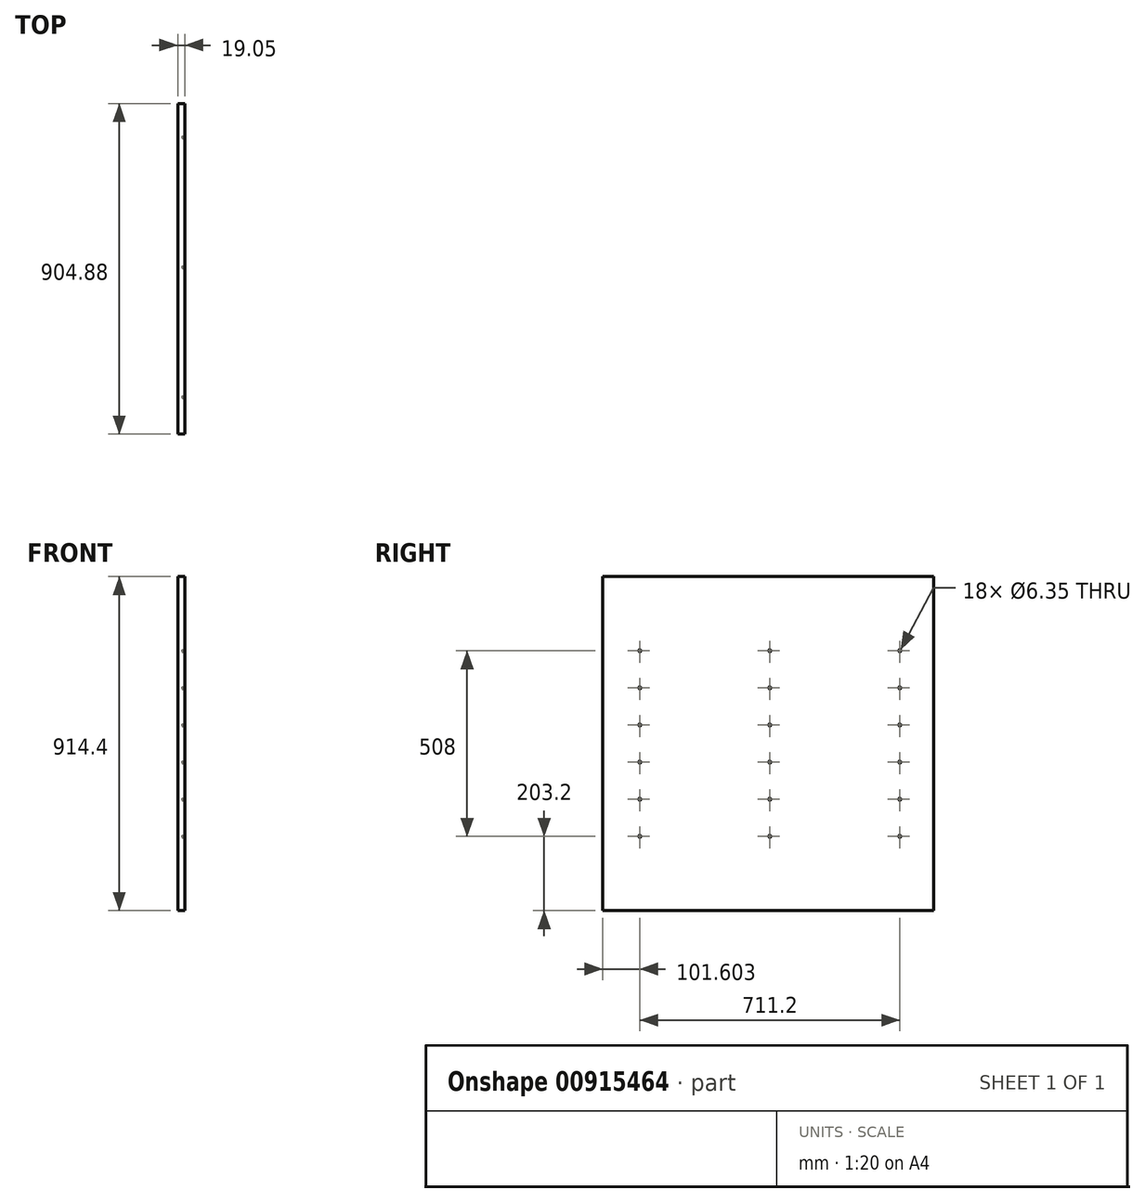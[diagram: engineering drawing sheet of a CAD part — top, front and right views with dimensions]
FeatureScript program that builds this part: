
annotation { "Feature Type Name" : "Feature", "Feature Type Description" : "" }
export const myFeature = defineFeature(function(context is Context, id is Id, definition is map)
    precondition{}
    {
        {
            var Q0;
            Q0=qCreatedBy(makeId("Right.planeOp"),FACE);
            var sketch = newSketch(context, id + "F0", { "sketchPlane" : qUnion([Q0])});
            skLineSegment(sketch, "E0.bottom", {"start": v(452.44, 457.2) * mm, "end": v(-452.44, 457.2) * mm});
            skLineSegment(sketch, "E0.top", {"start": v(452.44, -457.2) * mm, "end": v(-452.44, -457.2) * mm});
            skLineSegment(sketch, "E0.left", {"start": v(452.44, 457.2) * mm, "end": v(452.44, -457.2) * mm});
            skLineSegment(sketch, "E0.right", {"start": v(-452.44, 457.2) * mm, "end": v(-452.44, -457.2) * mm});
            skPoint(sketch, "E0.middle", {"position": v(0, 0) * mm});
            skSolve(sketch);
        }
        {
            var Q0;
            Q0=makeQuery(id+"F0.imprint","IMPRINT",FACE,{"disambiguationData":[TD([[makeQuery(id+"F0.imprint","IMPRINT",EDGE,{"derivedFrom":sQuery(id+"F0.wireOp",EDGE,"E0.bottom")}),1.0]])]});
            extrude(context, id + "F1", {"entities" : qUnion([Q0]), "oppositeDirection" : true, "depth" : 19.05 * mm, "offsetDistance" : 25.4 * mm});
        }
        {
            var Q0;
            Q0=makeQuery(id+"F1.opExtrude","CAP_FACE",FACE,{"disambiguationData":[OSD([sQuery(id+"F0.wireOp",EDGE,"E0.bottom"),sQuery(id+"F0.wireOp",EDGE,"E0.top"),sQuery(id+"F0.wireOp",EDGE,"E0.left"),sQuery(id+"F0.wireOp",EDGE,"E0.right")])],"isStart":true});
            var sketch = newSketch(context, id + "F2", { "sketchPlane" : qUnion([Q0])});
            skPoint(sketch, "E1", {"position": v(-350.84, 254) * mm});
            skPoint(sketch, "E2.0.1.0", {"position": v(-350.84, 152.4) * mm});
            skPoint(sketch, "E2.0.2.0", {"position": v(-350.84, 50.8) * mm});
            skPoint(sketch, "E2.0.3.0", {"position": v(-350.84, -50.8) * mm});
            skPoint(sketch, "E2.0.4.0", {"position": v(-350.84, -152.4) * mm});
            skPoint(sketch, "E2.0.5.0", {"position": v(-350.84, -254) * mm});
            skPoint(sketch, "E2.1.0.0", {"position": v(4.76, 254) * mm});
            skPoint(sketch, "E2.1.1.0", {"position": v(4.76, 152.4) * mm});
            skPoint(sketch, "E2.1.2.0", {"position": v(4.76, 50.8) * mm});
            skPoint(sketch, "E2.1.3.0", {"position": v(4.76, -50.8) * mm});
            skPoint(sketch, "E2.1.4.0", {"position": v(4.76, -152.4) * mm});
            skPoint(sketch, "E2.1.5.0", {"position": v(4.76, -254) * mm});
            skPoint(sketch, "E2.2.0.0", {"position": v(360.36, 254) * mm});
            skPoint(sketch, "E2.2.1.0", {"position": v(360.36, 152.4) * mm});
            skPoint(sketch, "E2.2.2.0", {"position": v(360.36, 50.8) * mm});
            skPoint(sketch, "E2.2.3.0", {"position": v(360.36, -50.8) * mm});
            skPoint(sketch, "E2.2.4.0", {"position": v(360.36, -152.4) * mm});
            skPoint(sketch, "E2.2.5.0", {"position": v(360.36, -254) * mm});
            skLineSegment(sketch, "E2.direction1", {"start": v(-350.84, 254) * mm, "end": v(4.76, 254) * mm, "construction": true});
            skLineSegment(sketch, "E2.direction2", {"start": v(-350.84, 254) * mm, "end": v(-350.84, 152.4) * mm, "construction": true});
            skSolve(sketch);
        }
        {
            var Q0;
            Q0=sQuery(id+"F2.wireOp",VERTEX,"E2.2.5.0");
            var Q1;
            Q1=sQuery(id+"F2.wireOp",VERTEX,"E2.0.4.0");
            var Q2;
            Q2=sQuery(id+"F2.wireOp",VERTEX,"E2.2.0.0");
            var Q3;
            Q3=sQuery(id+"F2.wireOp",VERTEX,"E2.1.0.0");
            var Q4;
            Q4=sQuery(id+"F2.wireOp",VERTEX,"E2.2.4.0");
            var Q5;
            Q5=sQuery(id+"F2.wireOp",VERTEX,"E2.2.1.0");
            var Q6;
            Q6=sQuery(id+"F2.wireOp",VERTEX,"E2.0.5.0");
            var Q7;
            Q7=sQuery(id+"F2.wireOp",VERTEX,"E2.1.1.0");
            var Q8;
            Q8=sQuery(id+"F2.wireOp",VERTEX,"E2.2.3.0");
            var Q9;
            Q9=sQuery(id+"F2.wireOp",VERTEX,"E2.direction2.end");
            var Q10;
            Q10=sQuery(id+"F2.wireOp",VERTEX,"E2.2.2.0");
            var Q11;
            Q11=sQuery(id+"F2.wireOp",VERTEX,"E1");
            var Q12;
            Q12=sQuery(id+"F2.wireOp",VERTEX,"E2.1.4.0");
            var Q13;
            Q13=sQuery(id+"F2.wireOp",VERTEX,"E2.0.3.0");
            var Q14;
            Q14=sQuery(id+"F2.wireOp",VERTEX,"E2.1.3.0");
            var Q15;
            Q15=sQuery(id+"F2.wireOp",VERTEX,"E2.0.2.0");
            var Q16;
            Q16=sQuery(id+"F2.wireOp",VERTEX,"E2.1.2.0");
            var Q17;
            Q17=sQuery(id+"F2.wireOp",VERTEX,"E2.1.5.0");
            var Q18;
            Q18=makeQuery(id+"F1.opExtrude","SWEPT_BODY",BODY,{"disambiguationData":[OSD([sQuery(id+"F0.wireOp",EDGE,"E0.bottom"),sQuery(id+"F0.wireOp",EDGE,"E0.top"),sQuery(id+"F0.wireOp",EDGE,"E0.left"),sQuery(id+"F0.wireOp",EDGE,"E0.right")])]});
            hole(context, id + "F3", {"style" : HoleStyle.SIMPLE, "endStyle" : HoleEndStyle.BLIND, "holeDiameter" : 6.35 * mm, "majorDiameter" : 6.35 * mm, "holeDepth" : 6.35 * mm, "isTappedThrough" : true, "tappedDepth" : 12.7 * mm, "tapClearance" : 3, "startFromSketch" : true, "locations" : qUnion([Q0, Q1, Q2, Q3, Q4, Q5, Q6, Q7, Q8, Q9, Q10, Q11, Q12, Q13, Q14, Q15, Q16, Q17]), "scope" : qUnion([Q18])});
        }
    });
